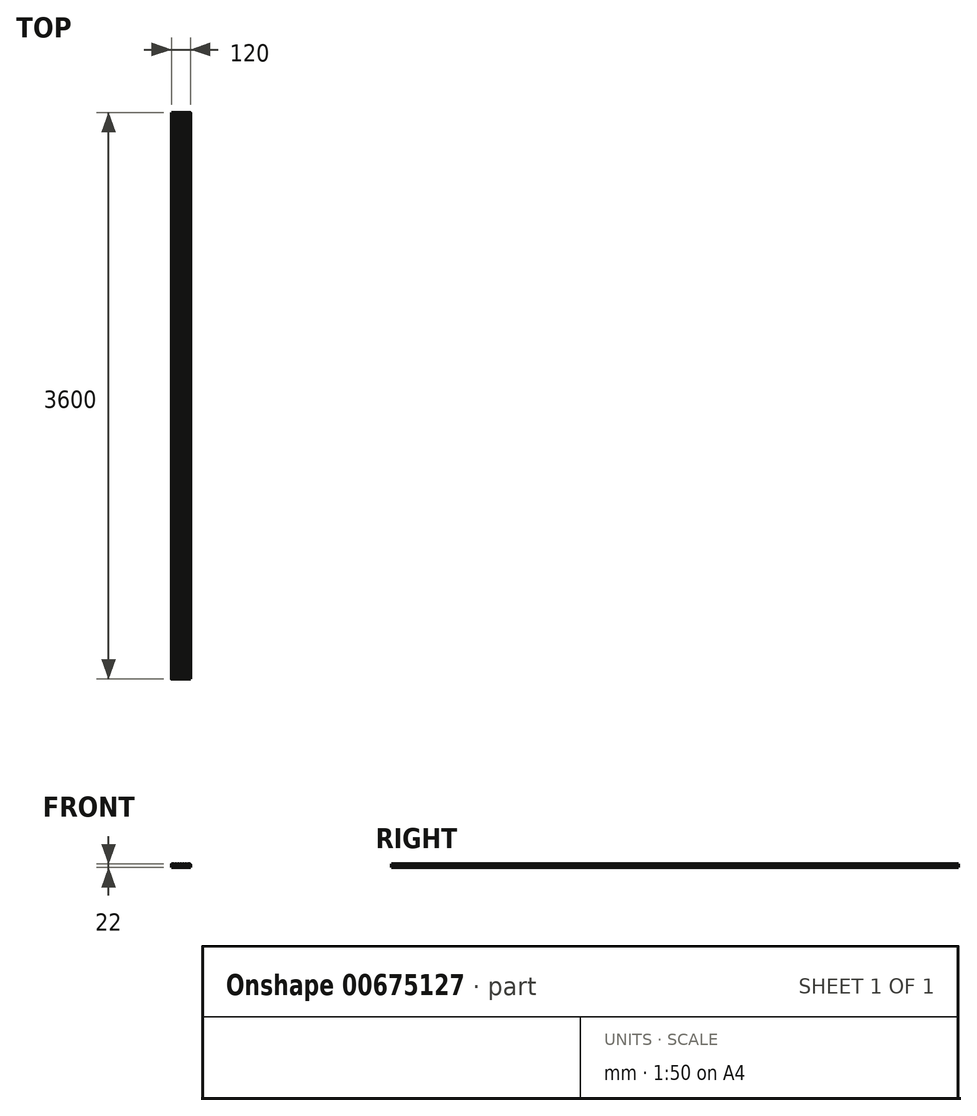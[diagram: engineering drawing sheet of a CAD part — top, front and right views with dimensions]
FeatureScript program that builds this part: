
annotation { "Feature Type Name" : "Feature", "Feature Type Description" : "" }
export const myFeature = defineFeature(function(context is Context, id is Id, definition is map)
    precondition{}
    {
        {
            var Q0;
            Q0=qCreatedBy(makeId("Front.planeOp"),FACE);
            var sketch = newSketch(context, id + "F0", { "sketchPlane" : qUnion([Q0])});
            skLineSegment(sketch, "E0.bottom", {"start": v(0, 0) * mm, "end": v(120, 0) * mm});
            skLineSegment(sketch, "E0.top", {"start": v(3, 22) * mm, "end": v(17.5, 22) * mm});
            skLineSegment(sketch, "E0.left", {"start": v(0, 0) * mm, "end": v(0, 19) * mm});
            skLineSegment(sketch, "E0.right", {"start": v(120, 0) * mm, "end": v(120, 19) * mm});
            skCircle(sketch, "E1", {"center": v(0, 22) * mm, "radius": 20 * mm, "construction": true});
            skArc(sketch, "E2", {"start": v(17.5, 22) * mm, "mid": v(20, 19.5) * mm, "end": v(22.5, 22) * mm});
            skArc(sketch, "E3.1.0.0", {"start": v(33.5, 22) * mm, "mid": v(36, 19.5) * mm, "end": v(38.5, 22) * mm});
            skArc(sketch, "E3.2.0.0", {"start": v(49.5, 22) * mm, "mid": v(52, 19.5) * mm, "end": v(54.5, 22) * mm});
            skArc(sketch, "E3.3.0.0", {"start": v(65.5, 22) * mm, "mid": v(68, 19.5) * mm, "end": v(70.5, 22) * mm});
            skArc(sketch, "E3.4.0.0", {"start": v(81.5, 22) * mm, "mid": v(84, 19.5) * mm, "end": v(86.5, 22) * mm});
            skLineSegment(sketch, "E3.direction1", {"start": v(22.5, 22) * mm, "end": v(33.5, 22) * mm});
            skArc(sketch, "E4.0.5.0", {"start": v(97.5, 22) * mm, "mid": v(100, 19.5) * mm, "end": v(102.5, 22) * mm});
            skArc(sketch, "E5.filletArc", {"start": v(3, 22) * mm, "mid": v(0.88, 21.12) * mm, "end": v(0, 19) * mm});
            skPoint(sketch, "E6.visualSharp", {"position": v(120, 22) * mm});
            skArc(sketch, "E6.filletArc", {"start": v(120, 19) * mm, "mid": v(119.12, 21.12) * mm, "end": v(117, 22) * mm});
            skLineSegment(sketch, "E7.trimOffspring", {"start": v(102.5, 22) * mm, "end": v(117, 22) * mm});
            skLineSegment(sketch, "E8.trimOffspring", {"start": v(86.5, 22) * mm, "end": v(97.5, 22) * mm});
            skLineSegment(sketch, "E9.trimOffspring", {"start": v(70.5, 22) * mm, "end": v(81.5, 22) * mm});
            skLineSegment(sketch, "E10.trimOffspring", {"start": v(54.5, 22) * mm, "end": v(65.5, 22) * mm});
            skLineSegment(sketch, "E11.trimOffspring", {"start": v(38.5, 22) * mm, "end": v(49.5, 22) * mm});
            skSolve(sketch);
        }
        {
            var Q0;
            Q0 = qSketchRegion(id + "F0", true);
            extrude(context, id + "F1", {"entities" : qUnion([Q0]), "depth" : 3600 * mm, "offsetDistance" : 25 * mm});
        }
    });
